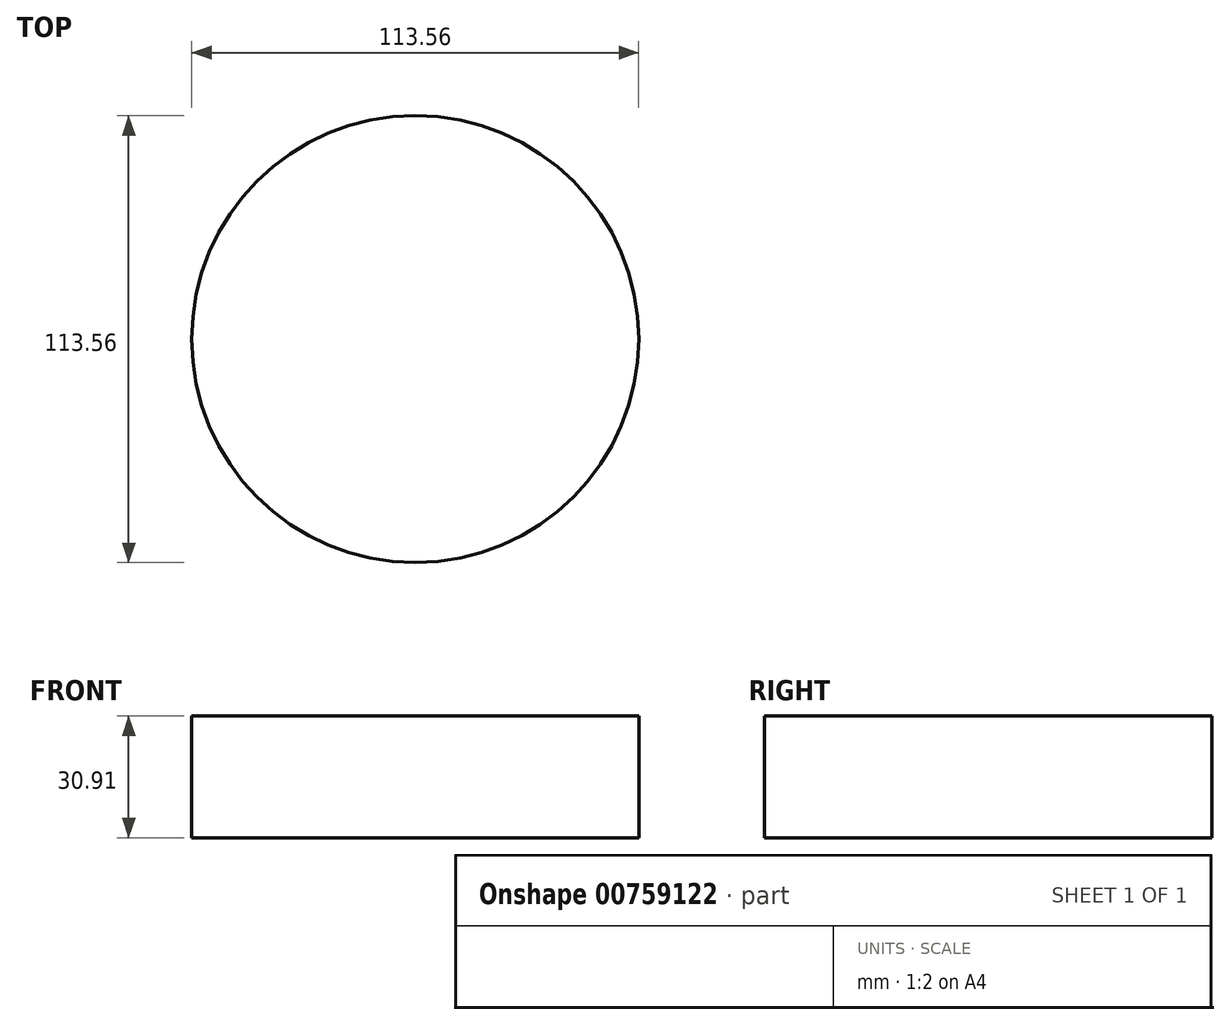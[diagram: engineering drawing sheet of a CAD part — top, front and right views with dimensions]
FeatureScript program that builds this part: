
annotation { "Feature Type Name" : "Feature", "Feature Type Description" : "" }
export const myFeature = defineFeature(function(context is Context, id is Id, definition is map)
    precondition{}
    {
        {
            var Q0;
            Q0=qCreatedBy(makeId("Top.planeOp"),FACE);
            var sketch = newSketch(context, id + "F0", { "sketchPlane" : qUnion([Q0])});
            skCircle(sketch, "E0", {"center": v(0, 0) * mm, "radius": 56.78 * mm});
            skSolve(sketch);
        }
        {
            var Q0;
            Q0 = qSketchRegion(id + "F0", true);
            extrude(context, id + "F1", {"entities" : qUnion([Q0]), "depth" : 30.9 * mm, "offsetDistance" : 25.4 * mm});
        }
    });
